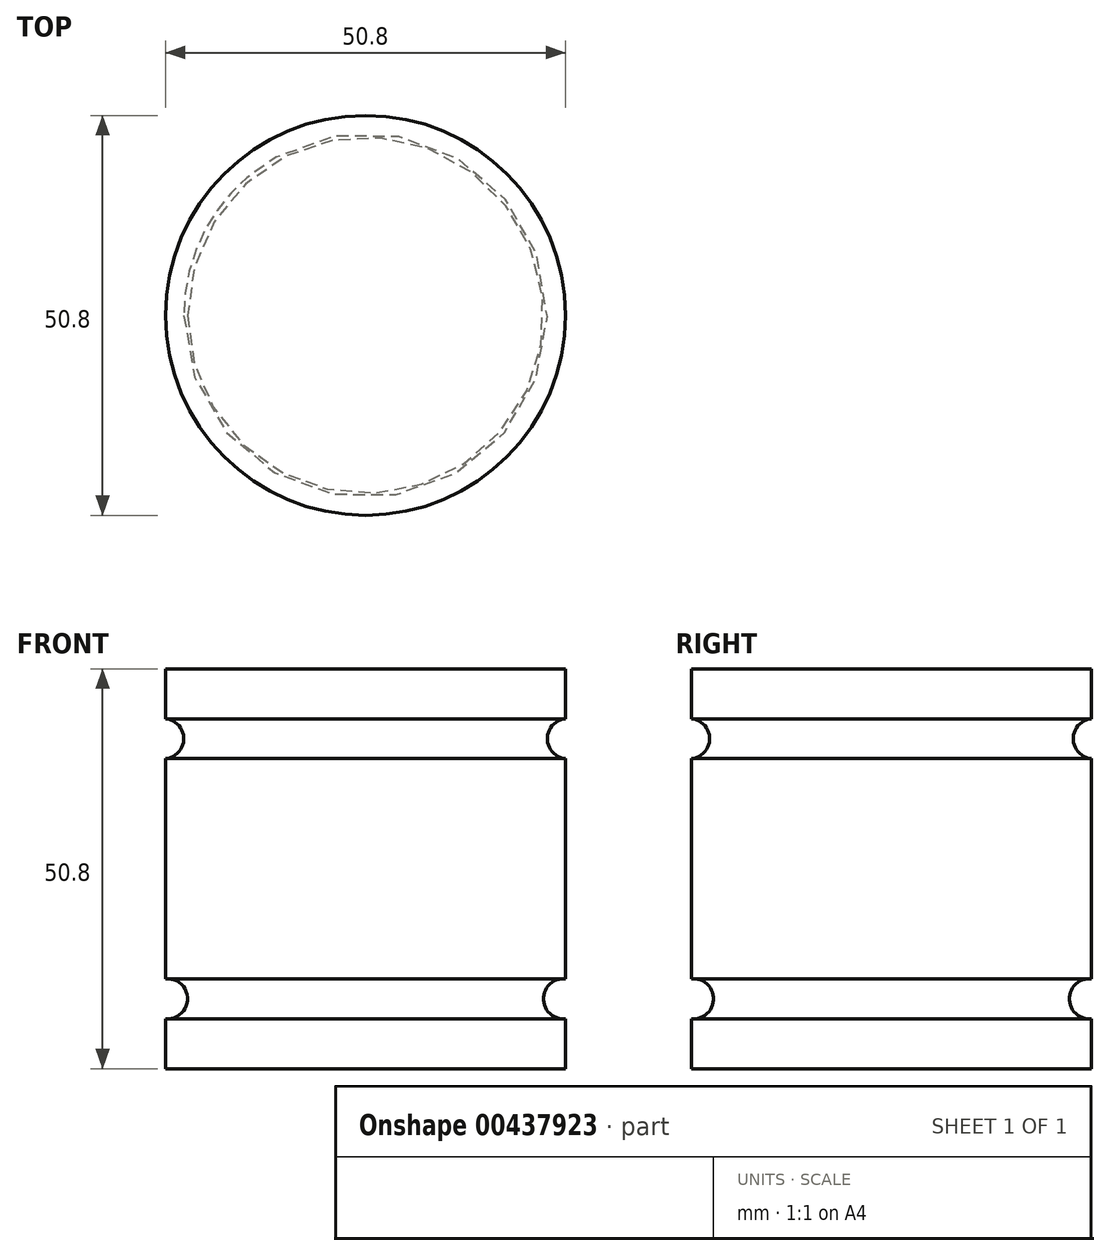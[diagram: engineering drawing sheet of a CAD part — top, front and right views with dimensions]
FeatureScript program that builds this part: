
annotation { "Feature Type Name" : "Feature", "Feature Type Description" : "" }
export const myFeature = defineFeature(function(context is Context, id is Id, definition is map)
    precondition{}
    {
        {
            var Q0;
            Q0=qCreatedBy(makeId("Front.planeOp"),FACE);
            var sketch = newSketch(context, id + "F0", { "sketchPlane" : qUnion([Q0])});
            skLineSegment(sketch, "E0", {"start": v(0, 0) * mm, "end": v(-25.4, 0) * mm});
            skLineSegment(sketch, "E1", {"start": v(-25.4, 0) * mm, "end": v(-25.4, 50.8) * mm});
            skLineSegment(sketch, "E2", {"start": v(-25.4, 50.8) * mm, "end": v(0, 50.8) * mm});
            skLineSegment(sketch, "E3", {"start": v(0, 50.8) * mm, "end": v(0, 44.45) * mm});
            skLineSegment(sketch, "E4", {"start": v(0, 0) * mm, "end": v(0, 6.35) * mm});
            skArc(sketch, "E5", {"start": v(0, 44.45) * mm, "mid": v(-2.31, 41.92) * mm, "end": v(0, 39.4) * mm});
            skArc(sketch, "E6", {"start": v(0, 11.4) * mm, "mid": v(-2.8, 8.88) * mm, "end": v(0, 6.35) * mm});
            skLineSegment(sketch, "E7", {"start": v(0, 11.4) * mm, "end": v(0, 39.4) * mm});
            skSolve(sketch);
        }
        {
            var Q0;
            Q0 = qSketchRegion(id + "F0", true);
            var Q1;
            Q1=sQuery(id+"F0.wireOp",EDGE,"E1");
            revolve(context, id + "F1", {"entities" : qUnion([Q0]), "axis" : qUnion([Q1]), "revolveType" : RevolveType.FULL});
        }
    });
